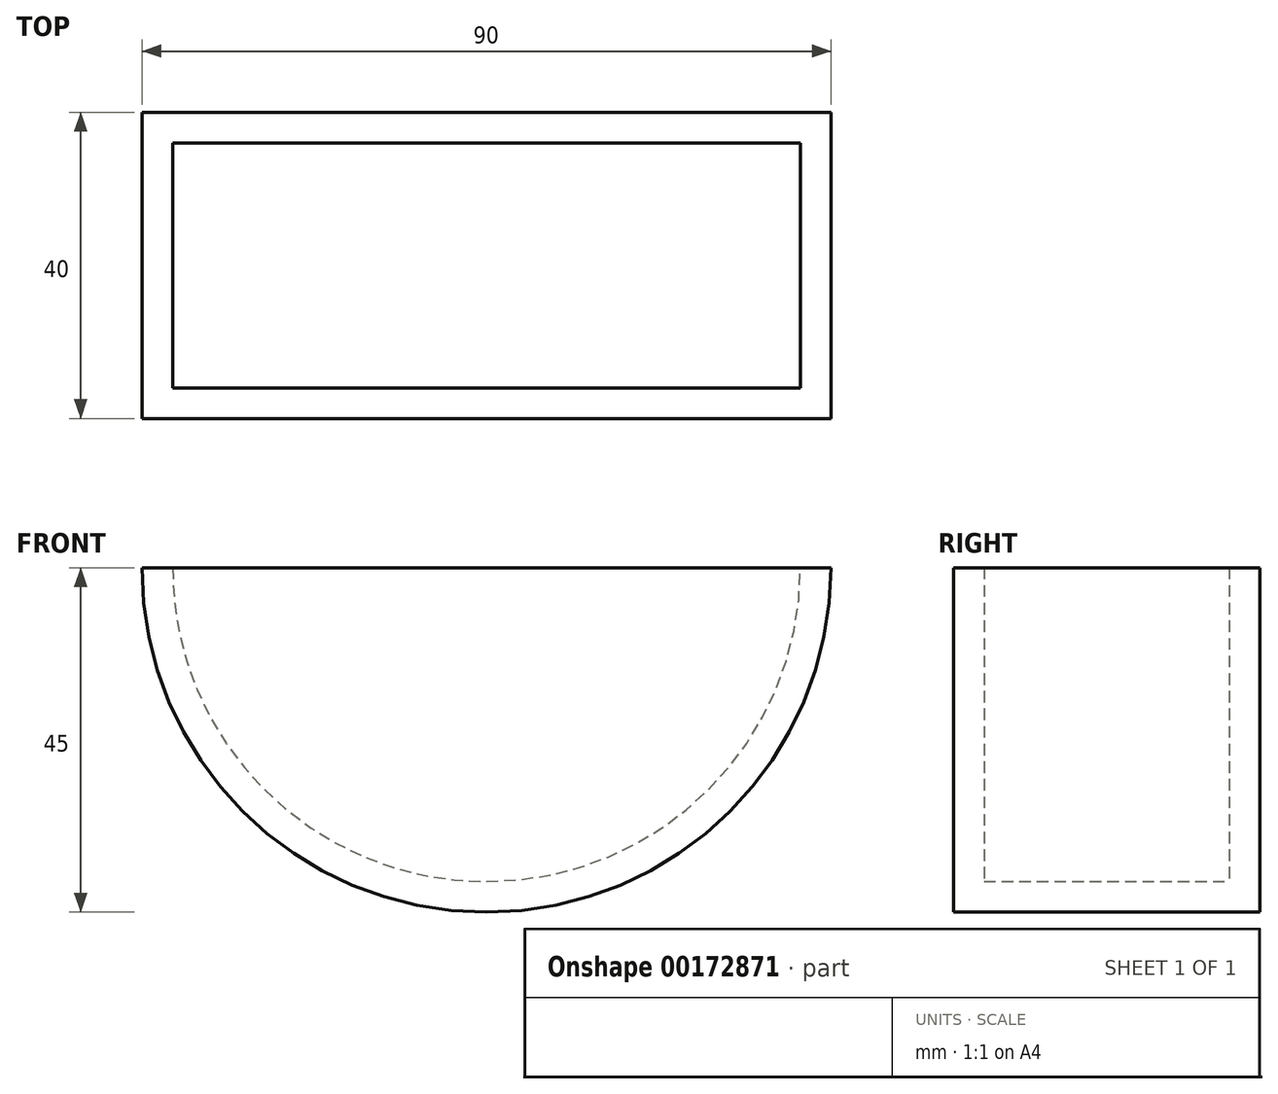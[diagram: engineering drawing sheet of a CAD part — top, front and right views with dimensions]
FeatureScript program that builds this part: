
annotation { "Feature Type Name" : "Feature", "Feature Type Description" : "" }
export const myFeature = defineFeature(function(context is Context, id is Id, definition is map)
    precondition{}
    {
        {
            var Q0;
            Q0=qCreatedBy(makeId("Front.planeOp"),FACE);
            var sketch = newSketch(context, id + "F0", { "sketchPlane" : qUnion([Q0])});
            skArc(sketch, "E0", {"start": v(-45.3, 0) * mm, "mid": v(-0.3, -45) * mm, "end": v(44.7, 0) * mm});
            skLineSegment(sketch, "E1", {"start": v(-45.3, 0) * mm, "end": v(44.7, 0) * mm});
            skSolve(sketch);
        }
        {
            var Q0;
            Q0=makeQuery(id+"F0.imprint","IMPRINT",FACE,{"disambiguationData":[TD([[makeQuery(id+"F0.imprint","IMPRINT",EDGE,{"derivedFrom":sQuery(id+"F0.wireOp",EDGE,"E0")}),1.0]])]});
            extrude(context, id + "F1", {"entities" : qUnion([Q0]), "depth" : 40 * mm});
        }
        {
            var Q0;
            Q0=makeQuery(id+"F1.opExtrude","SWEPT_FACE",FACE,{"disambiguationData":[OSD([sQuery(id+"F0.wireOp",EDGE,"E1")])]});
            shell(context, id + "F2", {"entities" : qUnion([Q0]), "thickness" : 4 * mm});
        }
    });
